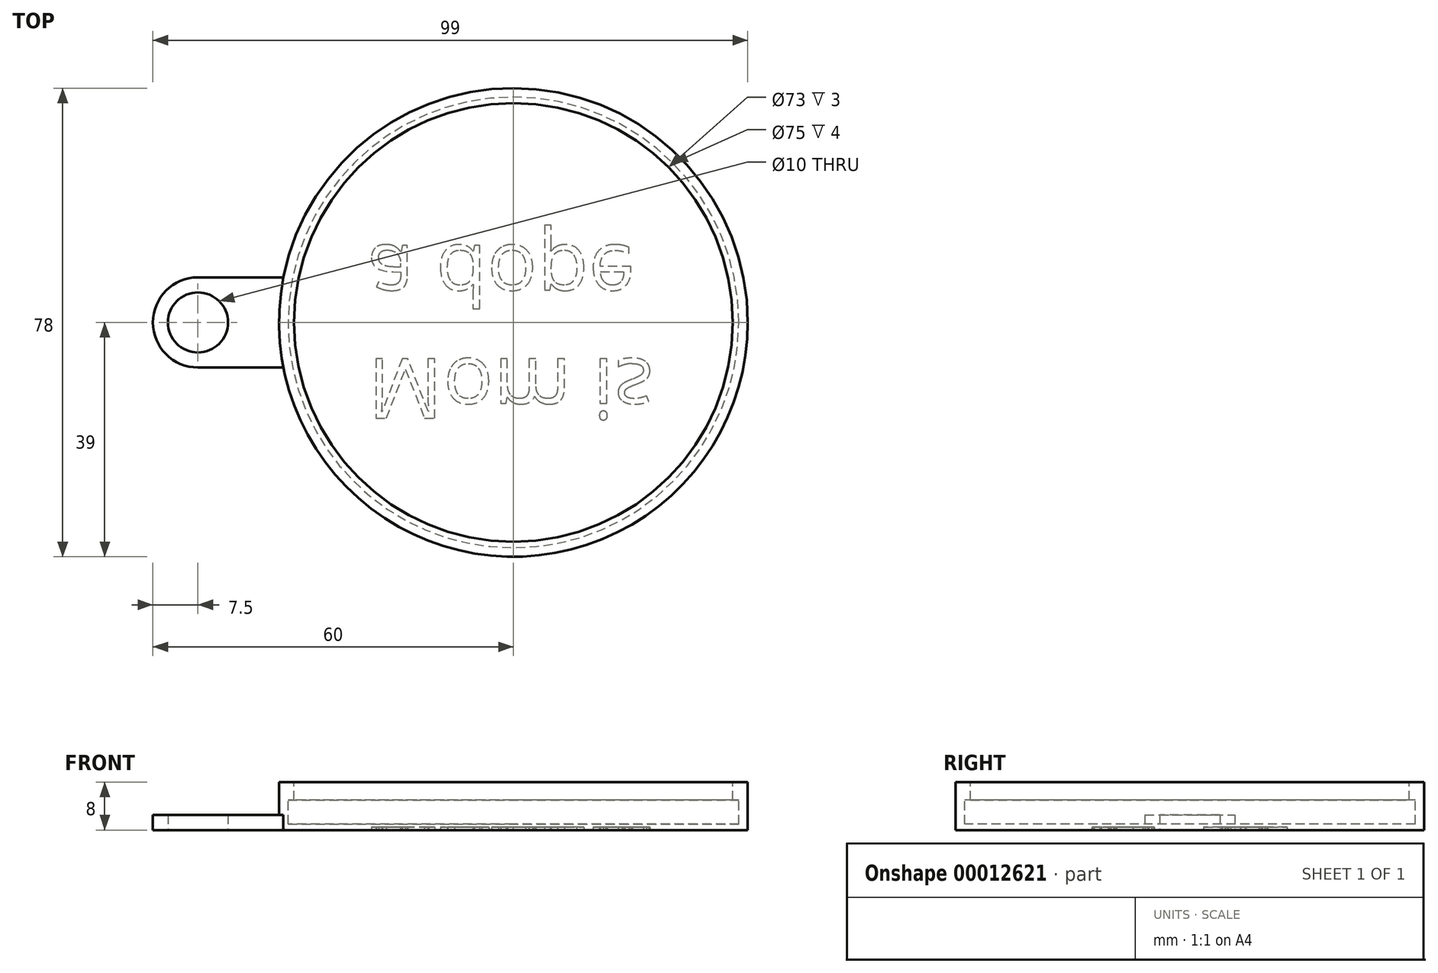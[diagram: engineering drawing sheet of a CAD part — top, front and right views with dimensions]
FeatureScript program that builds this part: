
annotation { "Feature Type Name" : "Feature", "Feature Type Description" : "" }
export const myFeature = defineFeature(function(context is Context, id is Id, definition is map)
    precondition{}
    {
        {
            var Q0;
            Q0=qCreatedBy(makeId("Top.planeOp"),FACE);
            var sketch = newSketch(context, id + "F0", { "sketchPlane" : qUnion([Q0])});
            skCircle(sketch, "E0", {"center": v(0, 0) * mm, "radius": 39 * mm});
            skSolve(sketch);
        }
        {
            var Q0;
            Q0 = qSketchRegion(id + "F0", true);
            extrude(context, id + "F1", {"entities" : qUnion([Q0]), "depth" : 8 * mm});
        }
        {
            var Q0;
            Q0=makeQuery(id+"F1.opExtrude","CAP_FACE",FACE,{"disambiguationData":[OSD([sQuery(id+"F0.wireOp",EDGE,"E0")])],"isStart":false});
            var sketch = newSketch(context, id + "F2", { "sketchPlane" : qUnion([Q0])});
            skCircle(sketch, "E1", {"center": v(0, 0) * mm, "radius": 36.5 * mm});
            skSolve(sketch);
        }
        {
            var Q0;
            Q0 = qSketchRegion(id + "F2", true);
            extrude(context, id + "F3", {"entities" : qUnion([Q0]), "operationType" : NewBodyOperationType.REMOVE, "oppositeDirection" : true, "depth" : 7 * mm});
        }
        {
            var Q0;
            Q0=qCreatedBy(makeId("Right.planeOp"),FACE);
            var sketch = newSketch(context, id + "F4", { "sketchPlane" : qUnion([Q0])});
            skLineSegment(sketch, "E2.bottom", {"start": v(35.5, 5) * mm, "end": v(37.5, 5) * mm});
            skLineSegment(sketch, "E2.top", {"start": v(35.5, 1) * mm, "end": v(37.5, 1) * mm});
            skLineSegment(sketch, "E2.left", {"start": v(35.5, 5) * mm, "end": v(35.5, 1) * mm});
            skLineSegment(sketch, "E2.right", {"start": v(37.5, 5) * mm, "end": v(37.5, 1) * mm});
            skSolve(sketch);
        }
        {
            var Q0;
            Q0 = qSketchRegion(id + "F4", true);
            var Q1;
            Q1=makeQuery(id+"F3.boolean.opBoolean","COPY",EDGE,{"derivedFrom":makeQuery(id+"F3.opExtrude","CAP_EDGE",EDGE,{"disambiguationData":[OSD([sQuery(id+"F2.wireOp",EDGE,"E1")])],"isStart":false})});
            sweep(context, id + "F5", {"operationType" : NewBodyOperationType.REMOVE, "profiles" : qUnion([Q0]), "path" : qUnion([Q1])});
        }
        {
            var Q0;
            Q0=makeQuery(id+"F1.opExtrude","CAP_FACE",FACE,{"disambiguationData":[OSD([sQuery(id+"F0.wireOp",EDGE,"E0")])],"isStart":true});
            var sketch = newSketch(context, id + "F6", { "sketchPlane" : qUnion([Q0])});
            skLineSegment(sketch, "E3.rect.bottom", {"start": v(-52.5, -7.5) * mm, "end": v(-37.5, -7.5) * mm});
            skLineSegment(sketch, "E3.rect.top", {"start": v(-52.5, 7.5) * mm, "end": v(-37.5, 7.5) * mm});
            skLineSegment(sketch, "E3.rect.left", {"start": v(-52.5, -7.5) * mm, "end": v(-52.5, 7.5) * mm, "construction": true});
            skLineSegment(sketch, "E3.rect.right", {"start": v(-37.5, -7.5) * mm, "end": v(-37.5, 7.5) * mm});
            skPoint(sketch, "E3.rect.middle", {"position": v(-45, 0) * mm});
            skArc(sketch, "E4", {"start": v(-52.5, 7.5) * mm, "mid": v(-60, 0) * mm, "end": v(-52.5, -7.5) * mm});
            skCircle(sketch, "E5", {"center": v(-52.5, 0) * mm, "radius": 5 * mm});
            skSolve(sketch);
        }
        {
            var Q0;
            Q0 = qSketchRegion(id + "F6", true);
            extrude(context, id + "F7", {"entities" : qUnion([Q0]), "operationType" : NewBodyOperationType.ADD, "oppositeDirection" : true, "depth" : 2.5 * mm});
        }
        {
            var Q0;
            Q0=makeQuery(id+"F7.boolean.opBoolean","MERGE",FACE,{"derivedFrom":[makeQuery(id+"F1.opExtrude","CAP_FACE",FACE,{"disambiguationData":[OSD([sQuery(id+"F0.wireOp",EDGE,"E0")])],"isStart":true}),makeQuery(id+"F7.opExtrude","CAP_FACE",FACE,{"disambiguationData":[OSD([sQuery(id+"F6.wireOp",EDGE,"E3.rect.bottom"),sQuery(id+"F6.wireOp",EDGE,"E3.rect.top"),sQuery(id+"F6.wireOp",EDGE,"E3.rect.right"),sQuery(id+"F6.wireOp",EDGE,"E4"),sQuery(id+"F6.wireOp",EDGE,"E5")])],"isStart":true})]});
            var sketch = newSketch(context, id + "F8", { "sketchPlane" : qUnion([Q0])});
            skText(sketch, "E6", { "text": "Mom is \na dope", "fontName": "OpenSans-Regular.ttf"});
            const initialGuessF8  = {"E6": [-0.02425, 0.00605, 1, 0, 0.01]};
            skSetInitialGuess(sketch, initialGuessF8);
            skSolve(sketch);
        }
        {
            var Q0;
            Q0=makeQuery(id+"F8.imprint","IMPRINT",FACE,{"disambiguationData":[TD([[makeQuery(id+"F8.imprint","IMPRINT",EDGE,{"derivedFrom":sQuery(id+"F8.wireOp",EDGE,"E6.sketch_text.stroke-0")}),-1.0]])]});
            var Q1;
            Q1=makeQuery(id+"F8.imprint","IMPRINT",FACE,{"disambiguationData":[TD([[makeQuery(id+"F8.imprint","IMPRINT",EDGE,{"derivedFrom":sQuery(id+"F8.wireOp",EDGE,"E6.sketch_text.stroke-35")}),-1.0]])]});
            var Q2;
            Q2=makeQuery(id+"F8.imprint","IMPRINT",FACE,{"disambiguationData":[TD([[makeQuery(id+"F8.imprint","IMPRINT",EDGE,{"derivedFrom":sQuery(id+"F8.wireOp",EDGE,"E6.sketch_text.stroke-63")}),-1.0]])]});
            var Q3;
            Q3=makeQuery(id+"F8.imprint","IMPRINT",FACE,{"disambiguationData":[TD([[makeQuery(id+"F8.imprint","IMPRINT",EDGE,{"derivedFrom":sQuery(id+"F8.wireOp",EDGE,"E6.sketch_text.stroke-67")}),-1.0]])]});
            var Q4;
            Q4=makeQuery(id+"F8.imprint","IMPRINT",FACE,{"disambiguationData":[TD([[makeQuery(id+"F8.imprint","IMPRINT",EDGE,{"derivedFrom":sQuery(id+"F8.wireOp",EDGE,"E6.sketch_text.stroke-75")}),-1.0]])]});
            var Q5;
            Q5=makeQuery(id+"F8.imprint","IMPRINT",FACE,{"disambiguationData":[TD([[makeQuery(id+"F8.imprint","IMPRINT",EDGE,{"derivedFrom":sQuery(id+"F8.wireOp",EDGE,"E6.sketch_text.stroke-18")}),-1.0]])]});
            var Q6;
            Q6=makeQuery(id+"F8.imprint","IMPRINT",FACE,{"disambiguationData":[TD([[makeQuery(id+"F8.imprint","IMPRINT",EDGE,{"derivedFrom":sQuery(id+"F8.wireOp",EDGE,"E6.sketch_text.stroke-100")}),-1.0]])]});
            var Q7;
            Q7=makeQuery(id+"F8.imprint","IMPRINT",FACE,{"disambiguationData":[TD([[makeQuery(id+"F8.imprint","IMPRINT",EDGE,{"derivedFrom":sQuery(id+"F8.wireOp",EDGE,"E6.sketch_text.stroke-127")}),-1.0]])]});
            var Q8;
            Q8=makeQuery(id+"F8.imprint","IMPRINT",FACE,{"disambiguationData":[TD([[makeQuery(id+"F8.imprint","IMPRINT",EDGE,{"derivedFrom":sQuery(id+"F8.wireOp",EDGE,"E6.sketch_text.stroke-151")}),-1.0]])]});
            var Q9;
            Q9=makeQuery(id+"F8.imprint","IMPRINT",FACE,{"disambiguationData":[TD([[makeQuery(id+"F8.imprint","IMPRINT",EDGE,{"derivedFrom":sQuery(id+"F8.wireOp",EDGE,"E6.sketch_text.stroke-168")}),-1.0]])]});
            var Q10;
            Q10=makeQuery(id+"F8.imprint","IMPRINT",FACE,{"disambiguationData":[TD([[makeQuery(id+"F8.imprint","IMPRINT",EDGE,{"derivedFrom":sQuery(id+"F8.wireOp",EDGE,"E6.sketch_text.stroke-193")}),-1.0]])]});
            extrude(context, id + "F9", {"entities" : qUnion([Q0, Q1, Q2, Q3, Q4, Q5, Q6, Q7, Q8, Q9, Q10]), "operationType" : NewBodyOperationType.REMOVE, "oppositeDirection" : true, "depth" : 0.5 * mm});
        }
    });
